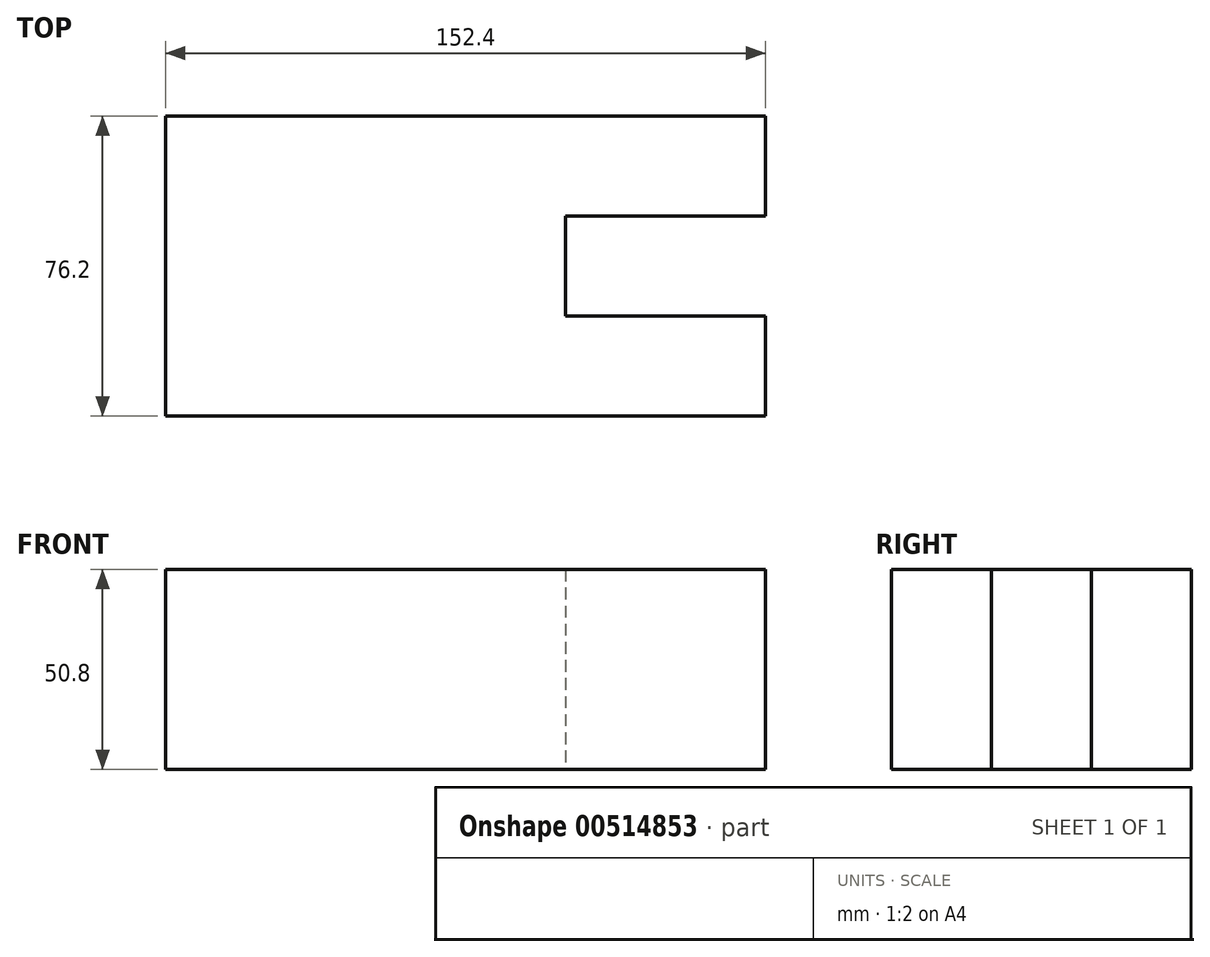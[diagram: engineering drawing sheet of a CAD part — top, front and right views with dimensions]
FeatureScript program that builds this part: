
annotation { "Feature Type Name" : "Feature", "Feature Type Description" : "" }
export const myFeature = defineFeature(function(context is Context, id is Id, definition is map)
    precondition{}
    {
        {
            var Q0;
            Q0=qCreatedBy(makeId("Top.planeOp"),FACE);
            var sketch = newSketch(context, id + "F0", { "sketchPlane" : qUnion([Q0])});
            skLineSegment(sketch, "E0", {"start": v(-73.75, 48.81) * mm, "end": v(78.65, 48.81) * mm});
            skLineSegment(sketch, "E1", {"start": v(78.65, 48.81) * mm, "end": v(78.65, 23.41) * mm});
            skLineSegment(sketch, "E2", {"start": v(78.65, 23.41) * mm, "end": v(27.85, 23.41) * mm});
            skLineSegment(sketch, "E3", {"start": v(27.85, 23.41) * mm, "end": v(27.85, -1.99) * mm});
            skLineSegment(sketch, "E4", {"start": v(27.85, -1.99) * mm, "end": v(78.65, -1.99) * mm});
            skLineSegment(sketch, "E5", {"start": v(78.65, -1.99) * mm, "end": v(78.65, -27.39) * mm});
            skLineSegment(sketch, "E6", {"start": v(78.65, -27.39) * mm, "end": v(-73.75, -27.39) * mm});
            skLineSegment(sketch, "E7", {"start": v(-73.75, -27.39) * mm, "end": v(-73.75, 48.81) * mm});
            skSolve(sketch);
        }
        {
            var Q0;
            Q0 = qSketchRegion(id + "F0", true);
            extrude(context, id + "F1", {"entities" : qUnion([Q0]), "depth" : 50.8 * mm, "offsetDistance" : 25.4 * mm});
        }
    });
